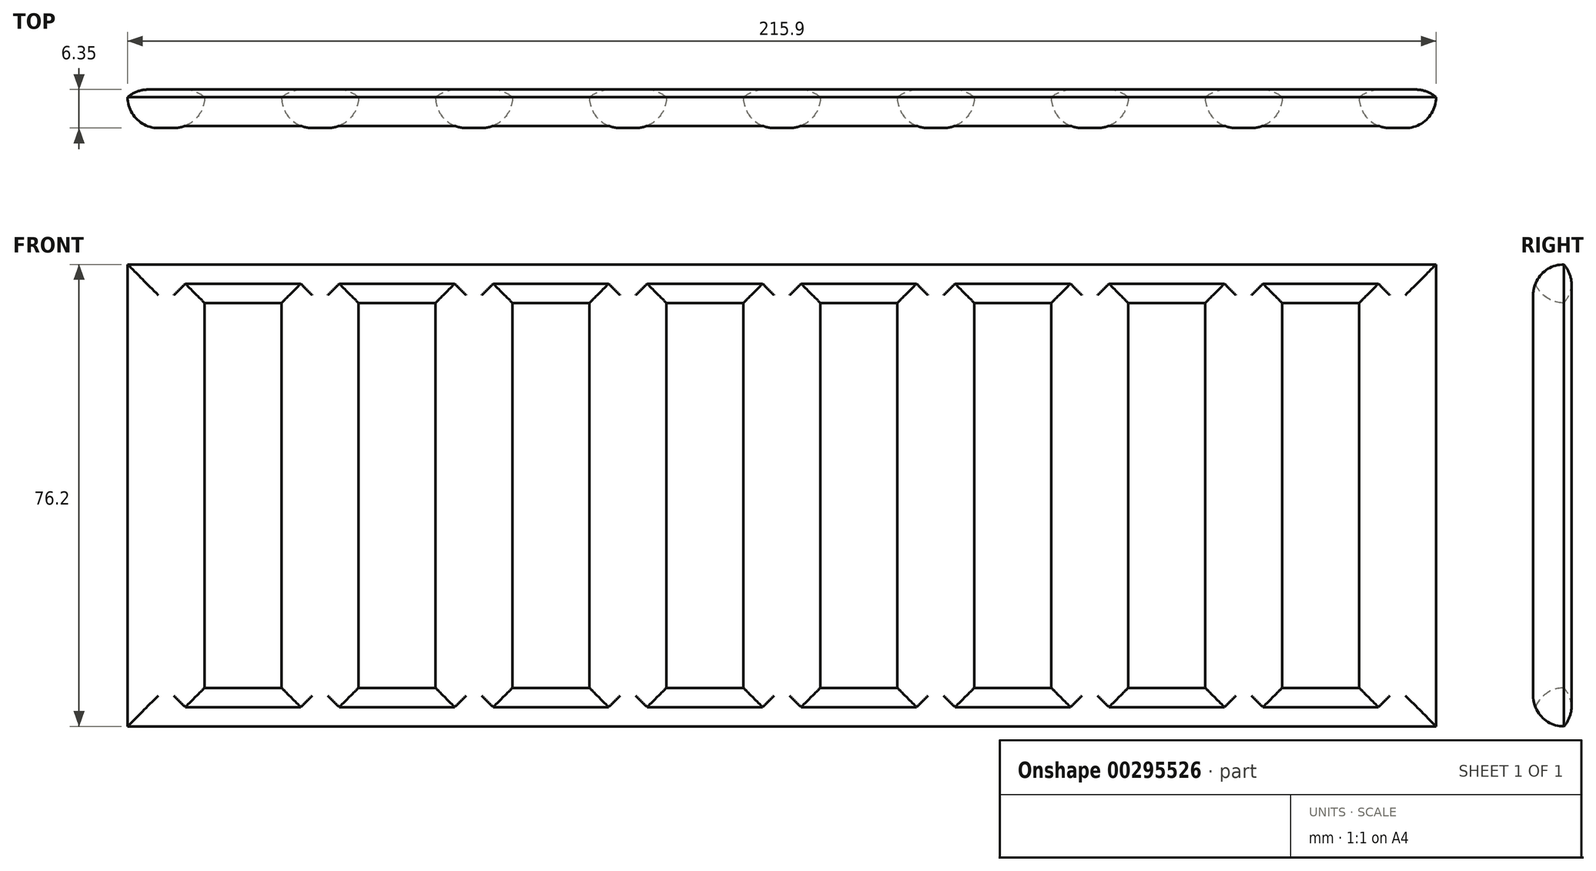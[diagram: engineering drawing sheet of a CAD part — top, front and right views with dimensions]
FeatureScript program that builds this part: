
annotation { "Feature Type Name" : "Feature", "Feature Type Description" : "" }
export const myFeature = defineFeature(function(context is Context, id is Id, definition is map)
    precondition{}
    {
        {
            var Q0;
            Q0=qCreatedBy(makeId("Front.planeOp"),FACE);
            var sketch = newSketch(context, id + "F0", { "sketchPlane" : qUnion([Q0])});
            skLineSegment(sketch, "E0.bottom", {"start": v(0, 0) * mm, "end": v(215.9, 0) * mm});
            skLineSegment(sketch, "E0.top", {"start": v(0, 76.2) * mm, "end": v(215.9, 76.2) * mm});
            skLineSegment(sketch, "E0.left", {"start": v(0, 0) * mm, "end": v(0, 76.2) * mm});
            skLineSegment(sketch, "E0.right", {"start": v(215.9, 0) * mm, "end": v(215.9, 76.2) * mm});
            skLineSegment(sketch, "E1.bottom", {"start": v(0, 76.2) * mm, "end": v(12.7, 76.2) * mm});
            skLineSegment(sketch, "E1.top", {"start": v(0, 0) * mm, "end": v(12.7, 0) * mm});
            skLineSegment(sketch, "E1.left", {"start": v(0, 76.2) * mm, "end": v(0, 0) * mm});
            skLineSegment(sketch, "E1.right", {"start": v(12.7, 69.85) * mm, "end": v(12.7, 6.35) * mm});
            skLineSegment(sketch, "E2.bottom", {"start": v(25.4, 76.2) * mm, "end": v(38.1, 76.2) * mm});
            skLineSegment(sketch, "E2.top", {"start": v(25.4, 0) * mm, "end": v(38.1, 0) * mm});
            skLineSegment(sketch, "E2.left", {"start": v(25.4, 69.85) * mm, "end": v(25.4, 6.35) * mm});
            skLineSegment(sketch, "E2.right", {"start": v(38.1, 69.85) * mm, "end": v(38.1, 6.35) * mm});
            skLineSegment(sketch, "E3.bottom", {"start": v(50.8, 76.2) * mm, "end": v(63.5, 76.2) * mm});
            skLineSegment(sketch, "E3.top", {"start": v(50.8, 0) * mm, "end": v(63.5, 0) * mm});
            skLineSegment(sketch, "E3.left", {"start": v(50.8, 69.85) * mm, "end": v(50.8, 6.35) * mm});
            skLineSegment(sketch, "E3.right", {"start": v(63.5, 69.85) * mm, "end": v(63.5, 6.35) * mm});
            skLineSegment(sketch, "E4.bottom", {"start": v(76.2, 76.2) * mm, "end": v(88.9, 76.2) * mm});
            skLineSegment(sketch, "E4.top", {"start": v(76.2, 0) * mm, "end": v(88.9, 0) * mm});
            skLineSegment(sketch, "E4.left", {"start": v(76.2, 69.85) * mm, "end": v(76.2, 6.35) * mm});
            skLineSegment(sketch, "E4.right", {"start": v(88.9, 69.85) * mm, "end": v(88.9, 6.35) * mm});
            skLineSegment(sketch, "E5.bottom", {"start": v(101.6, 76.2) * mm, "end": v(114.3, 76.2) * mm});
            skLineSegment(sketch, "E5.top", {"start": v(101.6, 0) * mm, "end": v(114.3, 0) * mm});
            skLineSegment(sketch, "E5.left", {"start": v(101.6, 69.85) * mm, "end": v(101.6, 6.35) * mm});
            skLineSegment(sketch, "E5.right", {"start": v(114.3, 69.85) * mm, "end": v(114.3, 6.35) * mm});
            skLineSegment(sketch, "E6.bottom", {"start": v(127, 76.2) * mm, "end": v(139.7, 76.2) * mm});
            skLineSegment(sketch, "E6.top", {"start": v(127, 0) * mm, "end": v(139.7, 0) * mm});
            skLineSegment(sketch, "E6.left", {"start": v(127, 69.85) * mm, "end": v(127, 6.35) * mm});
            skLineSegment(sketch, "E6.right", {"start": v(139.7, 69.85) * mm, "end": v(139.7, 6.35) * mm});
            skLineSegment(sketch, "E7.bottom", {"start": v(152.4, 76.2) * mm, "end": v(165.1, 76.2) * mm});
            skLineSegment(sketch, "E7.top", {"start": v(152.4, 0) * mm, "end": v(165.1, 0) * mm});
            skLineSegment(sketch, "E7.left", {"start": v(152.4, 69.85) * mm, "end": v(152.4, 6.35) * mm});
            skLineSegment(sketch, "E7.right", {"start": v(165.1, 69.85) * mm, "end": v(165.1, 6.35) * mm});
            skLineSegment(sketch, "E8.bottom", {"start": v(177.8, 76.2) * mm, "end": v(190.5, 76.2) * mm});
            skLineSegment(sketch, "E8.top", {"start": v(177.8, 0) * mm, "end": v(190.5, 0) * mm});
            skLineSegment(sketch, "E8.left", {"start": v(177.8, 69.85) * mm, "end": v(177.8, 6.35) * mm});
            skLineSegment(sketch, "E8.right", {"start": v(190.5, 69.85) * mm, "end": v(190.5, 0) * mm});
            skLineSegment(sketch, "E9.bottom", {"start": v(190.5, 76.2) * mm, "end": v(203.2, 76.2) * mm});
            skLineSegment(sketch, "E9.top", {"start": v(190.5, 0) * mm, "end": v(203.2, 0) * mm});
            skLineSegment(sketch, "E9.left", {"start": v(190.5, 69.85) * mm, "end": v(190.5, 6.35) * mm});
            skLineSegment(sketch, "E9.right", {"start": v(203.2, 69.85) * mm, "end": v(203.2, 6.35) * mm});
            skLineSegment(sketch, "E10.top", {"start": v(12.7, 69.85) * mm, "end": v(25.4, 69.85) * mm});
            skLineSegment(sketch, "E10.left", {"start": v(0, 76.2) * mm, "end": v(0, 69.85) * mm});
            skLineSegment(sketch, "E10.right", {"start": v(215.9, 76.2) * mm, "end": v(215.9, 69.85) * mm});
            skLineSegment(sketch, "E11.top", {"start": v(12.7, 6.35) * mm, "end": v(25.4, 6.35) * mm});
            skLineSegment(sketch, "E11.left", {"start": v(0, 0) * mm, "end": v(0, 6.35) * mm});
            skLineSegment(sketch, "E11.right", {"start": v(215.9, 0) * mm, "end": v(215.9, 6.35) * mm});
            skLineSegment(sketch, "E12.trimOffspring", {"start": v(38.1, 69.85) * mm, "end": v(50.8, 69.85) * mm});
            skLineSegment(sketch, "E13.trimOffspring", {"start": v(38.1, 6.35) * mm, "end": v(50.8, 6.35) * mm});
            skLineSegment(sketch, "E14.trimOffspring", {"start": v(63.5, 69.85) * mm, "end": v(76.2, 69.85) * mm});
            skLineSegment(sketch, "E15.trimOffspring", {"start": v(88.9, 69.85) * mm, "end": v(101.6, 69.85) * mm});
            skLineSegment(sketch, "E16.trimOffspring", {"start": v(114.3, 69.85) * mm, "end": v(127, 69.85) * mm});
            skLineSegment(sketch, "E17.trimOffspring", {"start": v(139.7, 69.85) * mm, "end": v(152.4, 69.85) * mm});
            skLineSegment(sketch, "E18.trimOffspring", {"start": v(165.1, 69.85) * mm, "end": v(177.8, 69.85) * mm});
            skLineSegment(sketch, "E19.trimOffspring", {"start": v(190.5, 69.85) * mm, "end": v(203.2, 69.85) * mm});
            skLineSegment(sketch, "E20.trimOffspring", {"start": v(190.5, 6.35) * mm, "end": v(203.2, 6.35) * mm});
            skLineSegment(sketch, "E21.trimOffspring", {"start": v(165.1, 6.35) * mm, "end": v(177.8, 6.35) * mm});
            skLineSegment(sketch, "E22.trimOffspring", {"start": v(139.7, 6.35) * mm, "end": v(152.4, 6.35) * mm});
            skLineSegment(sketch, "E23.trimOffspring", {"start": v(114.3, 6.35) * mm, "end": v(127, 6.35) * mm});
            skLineSegment(sketch, "E24.trimOffspring", {"start": v(88.9, 6.35) * mm, "end": v(101.6, 6.35) * mm});
            skLineSegment(sketch, "E25.trimOffspring", {"start": v(63.5, 6.35) * mm, "end": v(76.2, 6.35) * mm});
            skSolve(sketch);
        }
        {
            var Q0;
            Q0=makeQuery(id+"F0.imprint","IMPRINT",FACE,{"disambiguationData":[TD([[makeQuery(id+"F0.imprint","IMPRINT",EDGE,{"derivedFrom":sQuery(id+"F0.wireOp",EDGE,"E0.right")}),1.0]])]});
            extrude(context, id + "F1", {"entities" : qUnion([Q0]), "depth" : 6.35 * mm});
        }
        {
            var Q0;
            Q0=makeQuery(id+"F1.opExtrude","CAP_FACE",FACE,{"disambiguationData":[OSD([sQuery(id+"F0.wireOp",EDGE,"E0.right"),sQuery(id+"F0.wireOp",EDGE,"E1.left"),sQuery(id+"F0.wireOp",EDGE,"E1.right"),sQuery(id+"F0.wireOp",EDGE,"E2.left"),sQuery(id+"F0.wireOp",EDGE,"E2.right"),sQuery(id+"F0.wireOp",EDGE,"E3.left"),sQuery(id+"F0.wireOp",EDGE,"E3.right"),sQuery(id+"F0.wireOp",EDGE,"E4.left"),sQuery(id+"F0.wireOp",EDGE,"E4.right"),sQuery(id+"F0.wireOp",EDGE,"E5.left"),sQuery(id+"F0.wireOp",EDGE,"E5.right"),sQuery(id+"F0.wireOp",EDGE,"E6.left"),sQuery(id+"F0.wireOp",EDGE,"E6.right"),sQuery(id+"F0.wireOp",EDGE,"E7.left"),sQuery(id+"F0.wireOp",EDGE,"E7.right"),sQuery(id+"F0.wireOp",EDGE,"E8.left"),sQuery(id+"F0.wireOp",EDGE,"E9.left"),sQuery(id+"F0.wireOp",EDGE,"E9.right"),sQuery(id+"F0.wireOp",EDGE,"E0.top"),sQuery(id+"F0.wireOp",EDGE,"E10.top"),sQuery(id+"F0.wireOp",EDGE,"E10.left"),sQuery(id+"F0.wireOp",EDGE,"E10.right"),sQuery(id+"F0.wireOp",EDGE,"E0.bottom"),sQuery(id+"F0.wireOp",EDGE,"E11.top"),sQuery(id+"F0.wireOp",EDGE,"E11.left"),sQuery(id+"F0.wireOp",EDGE,"E11.right"),sQuery(id+"F0.wireOp",EDGE,"E12.trimOffspring"),sQuery(id+"F0.wireOp",EDGE,"E13.trimOffspring"),sQuery(id+"F0.wireOp",EDGE,"E14.trimOffspring"),sQuery(id+"F0.wireOp",EDGE,"E15.trimOffspring"),sQuery(id+"F0.wireOp",EDGE,"E16.trimOffspring"),sQuery(id+"F0.wireOp",EDGE,"E17.trimOffspring"),sQuery(id+"F0.wireOp",EDGE,"E18.trimOffspring"),sQuery(id+"F0.wireOp",EDGE,"E19.trimOffspring"),sQuery(id+"F0.wireOp",EDGE,"E20.trimOffspring"),sQuery(id+"F0.wireOp",EDGE,"E21.trimOffspring"),sQuery(id+"F0.wireOp",EDGE,"E22.trimOffspring"),sQuery(id+"F0.wireOp",EDGE,"E23.trimOffspring"),sQuery(id+"F0.wireOp",EDGE,"E24.trimOffspring"),sQuery(id+"F0.wireOp",EDGE,"E25.trimOffspring")])],"isStart":false});
            fillet(context, id + "F2", {"entities" : qUnion([Q0]), "radius" : 5.08 * mm, "tangentPropagation" : true, "allowEdgeOverflow" : false});
        }
        {
            var Q0;
            Q0=makeQuery(id+"F1.opExtrude","CAP_FACE",FACE,{"disambiguationData":[OSD([sQuery(id+"F0.wireOp",EDGE,"E0.right"),sQuery(id+"F0.wireOp",EDGE,"E1.left"),sQuery(id+"F0.wireOp",EDGE,"E1.right"),sQuery(id+"F0.wireOp",EDGE,"E2.left"),sQuery(id+"F0.wireOp",EDGE,"E2.right"),sQuery(id+"F0.wireOp",EDGE,"E3.left"),sQuery(id+"F0.wireOp",EDGE,"E3.right"),sQuery(id+"F0.wireOp",EDGE,"E4.left"),sQuery(id+"F0.wireOp",EDGE,"E4.right"),sQuery(id+"F0.wireOp",EDGE,"E5.left"),sQuery(id+"F0.wireOp",EDGE,"E5.right"),sQuery(id+"F0.wireOp",EDGE,"E6.left"),sQuery(id+"F0.wireOp",EDGE,"E6.right"),sQuery(id+"F0.wireOp",EDGE,"E7.left"),sQuery(id+"F0.wireOp",EDGE,"E7.right"),sQuery(id+"F0.wireOp",EDGE,"E8.left"),sQuery(id+"F0.wireOp",EDGE,"E9.left"),sQuery(id+"F0.wireOp",EDGE,"E9.right"),sQuery(id+"F0.wireOp",EDGE,"E0.top"),sQuery(id+"F0.wireOp",EDGE,"E10.top"),sQuery(id+"F0.wireOp",EDGE,"E10.left"),sQuery(id+"F0.wireOp",EDGE,"E10.right"),sQuery(id+"F0.wireOp",EDGE,"E0.bottom"),sQuery(id+"F0.wireOp",EDGE,"E11.top"),sQuery(id+"F0.wireOp",EDGE,"E11.left"),sQuery(id+"F0.wireOp",EDGE,"E11.right"),sQuery(id+"F0.wireOp",EDGE,"E12.trimOffspring"),sQuery(id+"F0.wireOp",EDGE,"E13.trimOffspring"),sQuery(id+"F0.wireOp",EDGE,"E14.trimOffspring"),sQuery(id+"F0.wireOp",EDGE,"E15.trimOffspring"),sQuery(id+"F0.wireOp",EDGE,"E16.trimOffspring"),sQuery(id+"F0.wireOp",EDGE,"E17.trimOffspring"),sQuery(id+"F0.wireOp",EDGE,"E18.trimOffspring"),sQuery(id+"F0.wireOp",EDGE,"E19.trimOffspring"),sQuery(id+"F0.wireOp",EDGE,"E20.trimOffspring"),sQuery(id+"F0.wireOp",EDGE,"E21.trimOffspring"),sQuery(id+"F0.wireOp",EDGE,"E22.trimOffspring"),sQuery(id+"F0.wireOp",EDGE,"E23.trimOffspring"),sQuery(id+"F0.wireOp",EDGE,"E24.trimOffspring"),sQuery(id+"F0.wireOp",EDGE,"E25.trimOffspring")])],"isStart":true});
            fillet(context, id + "F3", {"entities" : qUnion([Q0]), "radius" : 5.08 * mm, "tangentPropagation" : true, "allowEdgeOverflow" : false});
        }
    });
